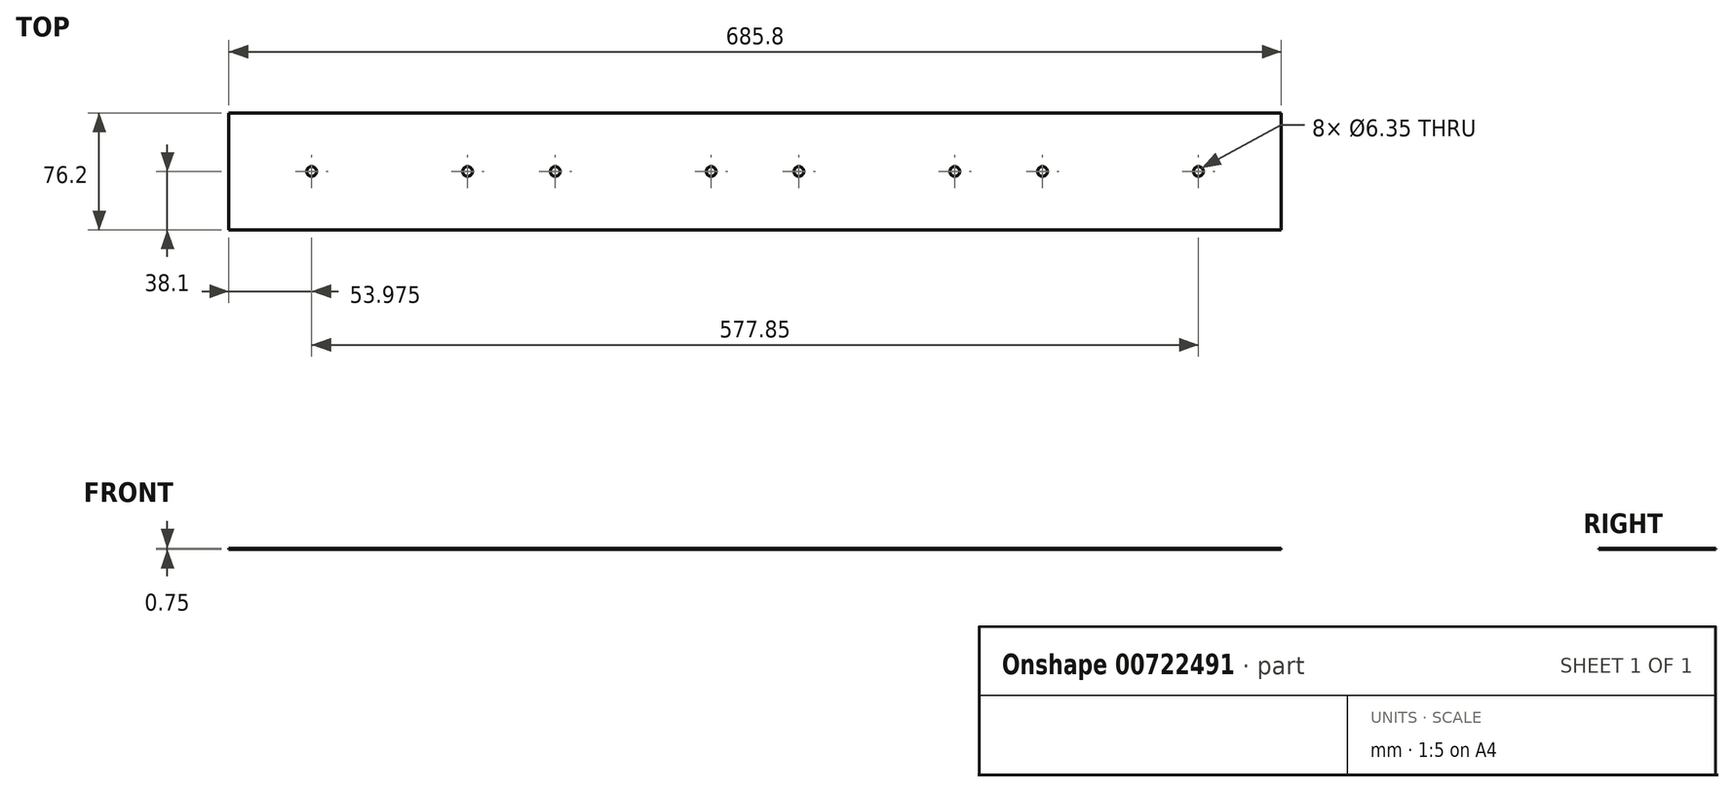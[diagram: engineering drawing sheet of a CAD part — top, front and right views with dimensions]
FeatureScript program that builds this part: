
annotation { "Feature Type Name" : "Feature", "Feature Type Description" : "" }
export const myFeature = defineFeature(function(context is Context, id is Id, definition is map)
    precondition{}
    {
        {
            assignVariable(context, id + "F0", {"name" : "T", "anyValue" : .75});
        }
        {
            var Q0;
            Q0=qCreatedBy(makeId("Top.planeOp"),FACE);
            var sketch = newSketch(context, id + "F1", { "sketchPlane" : qUnion([Q0])});
            skLineSegment(sketch, "E0.bottom", {"start": v(-342.9, 38.1) * mm, "end": v(342.9, 38.1) * mm});
            skLineSegment(sketch, "E0.top", {"start": v(-342.9, -38.1) * mm, "end": v(342.9, -38.1) * mm});
            skLineSegment(sketch, "E0.left", {"start": v(-342.9, 38.1) * mm, "end": v(-342.9, -38.1) * mm});
            skLineSegment(sketch, "E0.right", {"start": v(342.9, 38.1) * mm, "end": v(342.9, -38.1) * mm});
            skCircle(sketch, "E1", {"center": v(-288.93, 0) * mm, "radius": 3.18 * mm});
            skLineSegment(sketch, "E2", {"start": v(-342.9, 0) * mm, "end": v(342.9, 0) * mm, "construction": true});
            skLineSegment(sketch, "E3", {"start": v(0, 38.1) * mm, "end": v(0, -38.1) * mm, "construction": true});
            skCircle(sketch, "E4", {"center": v(-187.33, 0) * mm, "radius": 3.18 * mm});
            skCircle(sketch, "E5", {"center": v(-130.18, 0) * mm, "radius": 3.18 * mm});
            skCircle(sketch, "E6", {"center": v(-28.58, 0) * mm, "radius": 3.18 * mm});
            skCircle(sketch, "E7", {"center": v(28.58, 0) * mm, "radius": 3.18 * mm});
            skCircle(sketch, "E8", {"center": v(130.18, 0) * mm, "radius": 3.18 * mm});
            skCircle(sketch, "E9", {"center": v(187.33, 0) * mm, "radius": 3.18 * mm});
            skCircle(sketch, "E10", {"center": v(288.93, 0) * mm, "radius": 3.18 * mm});
            skSolve(sketch);
        }
        {
            var Q0;
            Q0 = qSketchRegion(id + "F1", true);
            extrude(context, id + "F2", {"entities" : qUnion([Q0]), "depth" : (getVariable(context, 'T')) * mm, "offsetDistance" : 25.4 * mm});
        }
    });
